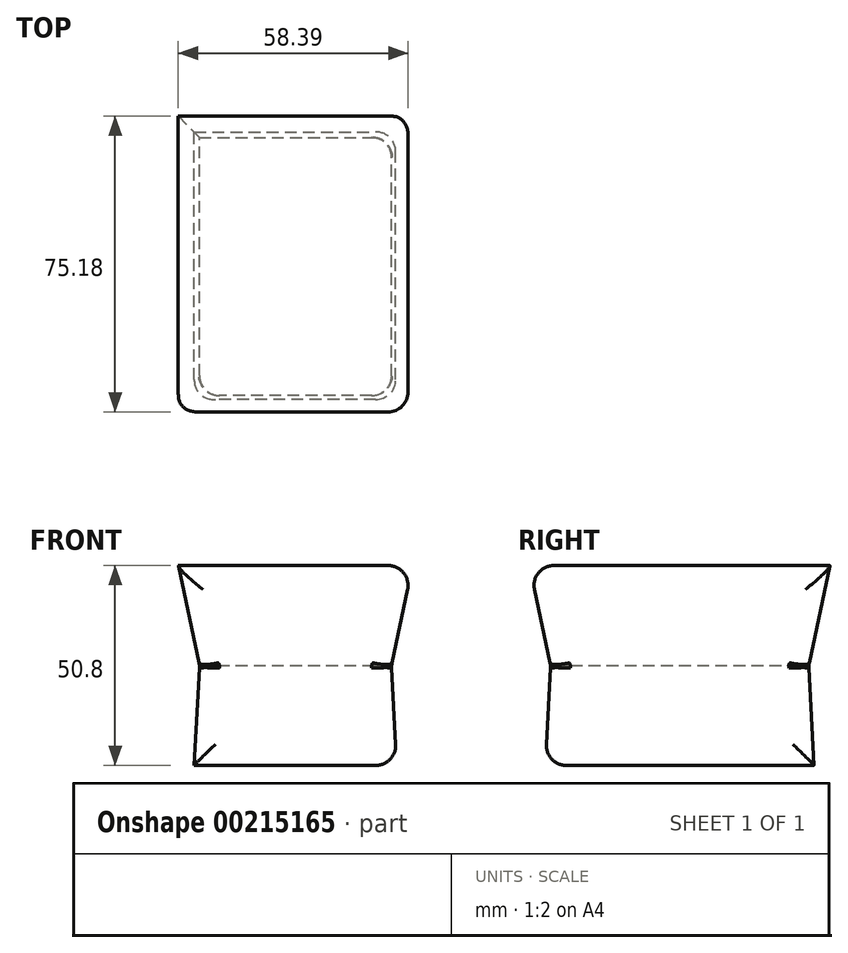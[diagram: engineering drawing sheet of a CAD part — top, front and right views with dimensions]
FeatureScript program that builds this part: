
annotation { "Feature Type Name" : "Feature", "Feature Type Description" : "" }
export const myFeature = defineFeature(function(context is Context, id is Id, definition is map)
    precondition{}
    {
        {
            var Q0;
            Q0=qCreatedBy(makeId("Top.planeOp"),FACE);
            var sketch = newSketch(context, id + "F0", { "sketchPlane" : qUnion([Q0])});
            skLineSegment(sketch, "E0.bottom", {"start": v(12.58, 22.74) * mm, "end": v(61.36, 22.74) * mm});
            skLineSegment(sketch, "E0.top", {"start": v(12.58, -42.84) * mm, "end": v(61.36, -42.84) * mm});
            skLineSegment(sketch, "E0.left", {"start": v(12.58, 22.74) * mm, "end": v(12.58, -42.84) * mm});
            skLineSegment(sketch, "E0.right", {"start": v(61.36, 22.74) * mm, "end": v(61.36, -42.84) * mm});
            skSolve(sketch);
        }
        {
            var Q0;
            Q0=makeQuery(id+"F0.imprint","IMPRINT",FACE,{"disambiguationData":[TD([[makeQuery(id+"F0.imprint","IMPRINT",EDGE,{"derivedFrom":sQuery(id+"F0.wireOp",EDGE,"E0.bottom")}),-1.0]])]});
            extrude(context, id + "F1", {"entities" : qUnion([Q0]), "depth" : 25.4 * mm, "offsetDistance" : 25.4 * mm, "hasDraft" : true, "draftAngle" : 12 * degree, "hasSecondDirection" : true, "secondDirectionOppositeDirection" : true, "secondDirectionDepth" : 25.4 * mm, "hasSecondDirectionDraft" : true, "secondDirectionDraftAngle" : 3 * degree});
        }
        {
            var Q0;
            Q0=makeQuery(id+"F1.*.split.splitOp","SPLIT",EDGE,{"derivedFrom":makeQuery(id+"F1.opExtrude","SWEPT_EDGE",EDGE,{"disambiguationData":[OSD([sQuery(id+"F0.wireOp",EDGE,"E0.top"),sQuery(id+"F0.wireOp",EDGE,"E0.right")])]})});
            var Q1;
            Q1=makeQuery(id+"F1.*.split.splitOp","SPLIT",FACE,{"derivedFrom":makeQuery(id+"F1.opExtrude","SWEPT_FACE",FACE,{"disambiguationData":[OSD([sQuery(id+"F0.wireOp",EDGE,"E0.top")])]})});
            var Q2;
            Q2=makeQuery(id+"F1.*.split.splitOp","SPLIT",FACE,{"derivedFrom":makeQuery(id+"F1.opExtrude","SWEPT_FACE",FACE,{"disambiguationData":[OSD([sQuery(id+"F0.wireOp",EDGE,"E0.top")])]}),"isFromBackBody":true});
            var Q3;
            Q3=makeQuery(id+"F1.*.split.splitOp","SPLIT",FACE,{"derivedFrom":makeQuery(id+"F1.opExtrude","SWEPT_FACE",FACE,{"disambiguationData":[OSD([sQuery(id+"F0.wireOp",EDGE,"E0.right")])]}),"isFromBackBody":true});
            var Q4;
            Q4=makeQuery(id+"F1.*.split.splitOp","SPLIT",FACE,{"derivedFrom":makeQuery(id+"F1.opExtrude","SWEPT_FACE",FACE,{"disambiguationData":[OSD([sQuery(id+"F0.wireOp",EDGE,"E0.right")])]})});
            fillet(context, id + "F2", {"entities" : qUnion([Q0, Q1, Q2, Q3, Q4]), "tangentPropagation" : true, "radius" : 5.08 * mm, "defaultsChanged" : false, "vertexSettings" : [], "allowEdgeOverflow" : false});
        }
    });
